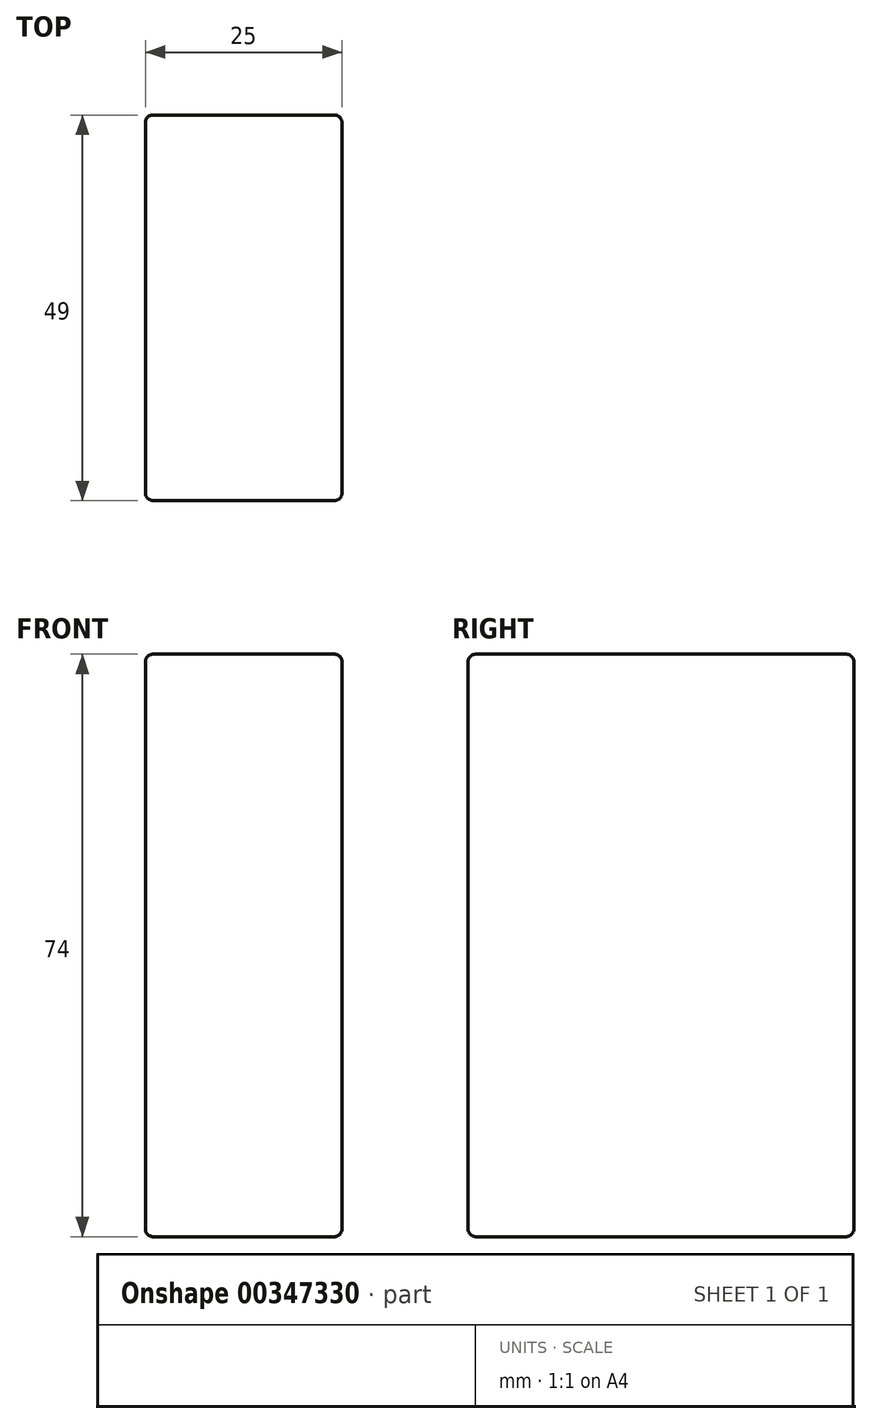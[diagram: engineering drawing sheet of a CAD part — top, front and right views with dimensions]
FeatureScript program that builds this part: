
annotation { "Feature Type Name" : "Feature", "Feature Type Description" : "" }
export const myFeature = defineFeature(function(context is Context, id is Id, definition is map)
    precondition{}
    {
        {
            var Q0;
            Q0=qCreatedBy(makeId("Top.planeOp"),FACE);
            var sketch = newSketch(context, id + "F0", { "sketchPlane" : qUnion([Q0])});
            skLineSegment(sketch, "E0.bottom", {"start": v(-12.5, -24.5) * mm, "end": v(12.5, -24.5) * mm});
            skLineSegment(sketch, "E0.top", {"start": v(-12.5, 24.5) * mm, "end": v(12.5, 24.5) * mm});
            skLineSegment(sketch, "E0.left", {"start": v(-12.5, -24.5) * mm, "end": v(-12.5, 24.5) * mm});
            skLineSegment(sketch, "E0.right", {"start": v(12.5, -24.5) * mm, "end": v(12.5, 24.5) * mm});
            skPoint(sketch, "E0.middle", {"position": v(0, 0) * mm});
            skSolve(sketch);
        }
        {
            var Q0;
            Q0 = qSketchRegion(id + "F0", true);
            extrude(context, id + "F1", {"entities" : qUnion([Q0]), "depth" : 74 * mm});
        }
        {
            var Q0;
            Q0=makeQuery(id+"F1.opExtrude","SWEPT_EDGE",EDGE,{"disambiguationData":[OSD([sQuery(id+"F0.wireOp",EDGE,"E0.bottom"),sQuery(id+"F0.wireOp",EDGE,"E0.right")])]});
            var Q1;
            Q1=makeQuery(id+"F1.opExtrude","SWEPT_FACE",FACE,{"disambiguationData":[OSD([sQuery(id+"F0.wireOp",EDGE,"E0.right")])]});
            var Q2;
            Q2=makeQuery(id+"F1.opExtrude","CAP_FACE",FACE,{"disambiguationData":[OSD([sQuery(id+"F0.wireOp",EDGE,"E0.bottom"),sQuery(id+"F0.wireOp",EDGE,"E0.top"),sQuery(id+"F0.wireOp",EDGE,"E0.left"),sQuery(id+"F0.wireOp",EDGE,"E0.right")])],"isStart":false});
            var Q3;
            Q3=makeQuery(id+"F1.opExtrude","SWEPT_FACE",FACE,{"disambiguationData":[OSD([sQuery(id+"F0.wireOp",EDGE,"E0.bottom")])]});
            var Q4;
            Q4=makeQuery(id+"F1.opExtrude","SWEPT_FACE",FACE,{"disambiguationData":[OSD([sQuery(id+"F0.wireOp",EDGE,"E0.top")])]});
            var Q5;
            Q5=makeQuery(id+"F1.opExtrude","SWEPT_FACE",FACE,{"disambiguationData":[OSD([sQuery(id+"F0.wireOp",EDGE,"E0.left")])]});
            fillet(context, id + "F2", {"entities" : qUnion([Q0, Q1, Q2, Q3, Q4, Q5]), "radius" : 1 * mm, "tangentPropagation" : true, "allowEdgeOverflow" : false});
        }
    });
